# Revit family: WAP-Enclosure_Indoor_Ventev_2x2x4in-CTEN
name_source: partatom
category: Generic Models
units: mm (PartAtom-declared; Revit-internal decimal feet)

## family parameters
Can host rebar = No
Cut with Voids When Loaded = No
Host = Face
Maintain Annotation Orientation = No
OmniClass Number = 23.85.50.00
OmniClass Title = Communication Systems
Part Type = Normal
Room Calculation Point = No
Round Connector Dimension = Use Diameter
Shared = No

## types (9) — shared parameters
Assembly Code = D5030600
Construction Details = http://www.arcat.com
Default Elevation = 0' - 0"
Keynote = 27 20 00
Manufacturer = Ventev Innovations
Manufacturer Website = http://www.terra-wave.com
Product Data = http://www.arcat.com
Revision = R1_2016-12
Sales Information = http://www.terra-wave.com
Standards Conformance = NEC300-22 and 300-23
URL = http://www.terra-wave.com
Unit Depth = 0' - 4"
Unit Length = 1' - 11 3/4"
Unit Width = 1' - 11 3/4"
zero-valued in all types: Expected Lifespan (Years), Maintenance Schedule (Months), Warranty Duration (Years)

## per-type parameters (varying)
| type | Accent Material | Description | Door Design | Model |
| CISCO 2700 3700 Interchangeable | Plastic - Ventev - White | Ventev Ceiling Tile WAP Enclosure - CTEN-2x2-ID-CISCO as Specified | CTENDoor_CISCO : CISCO 2700 3700 | CTEN-2x2-ID-CISCO |
| CISCO 2600 3600 Interchangeable | Plastic - Ventev - White | Ventev Ceiling Tile WAP Enclosure - CTEN-2x2-ID-CISCO as Specified | CTENDoor_CISCO : CISCO 2600 3600 | CTEN-2x2-ID-CISCO |
| Aruba325 Interchangeable | Plastic - Ventev - White | Ventev Ceiling Tile WAP Enclosure - CTEN-2x2-ID-AP325 as Specified | CTENDoor_Aruba | CTEN-2x2-ID-AP325 |
| HALO Interchangeable | Plastic - Ventev - White | Ventev Ceiling Tile WAP Enclosure - CTEN-2x2-ID-HALO as Specified | CTENDoor_HALO | CTEN-2x2-ID-HALO |
| Meraki Interchangeable | Plastic - Ventev - White | Ventev Ceiling Tile WAP Enclosure - CTEN-2x2-ID-MR34 as Specified | CTENDoor_Meraki | CTEN-2x2-ID-MR34 |
| Bubble Clear Interchangeable | Plastic - Ventev - Clear | Ventev Ceiling Tile WAP Enclosure - CTEN-2x2-ID11113C as Specified | CTENDoor_Bubble | CTEN-2x2-ID11113C |
| Bubble White Interchangeable | Plastic - Ventev - White | Ventev Ceiling Tile WAP Enclosure - CTEN-2x2-ID11113W as Specified | CTENDoor_Bubble | CTEN-2x2-ID11113W |
| Clear Bubble | Plastic - Ventev - Clear | Ventev Ceiling Tile WAP Enclosure - CTEN-2x2-11113F-C as Specified | CTENDoor_Bubble | CTEN-2x2-11113F-C |
| White Bubble | Plastic - Ventev - White | Ventev Ceiling Tile WAP Enclosure - CTEN-2x2-11113F-W as Specified | CTENDoor_Bubble | CTEN-2x2-11113F-W |

## geometry (parser evidence)
native form markers: Sweep x13
no freeform markers — native parametric forms only
